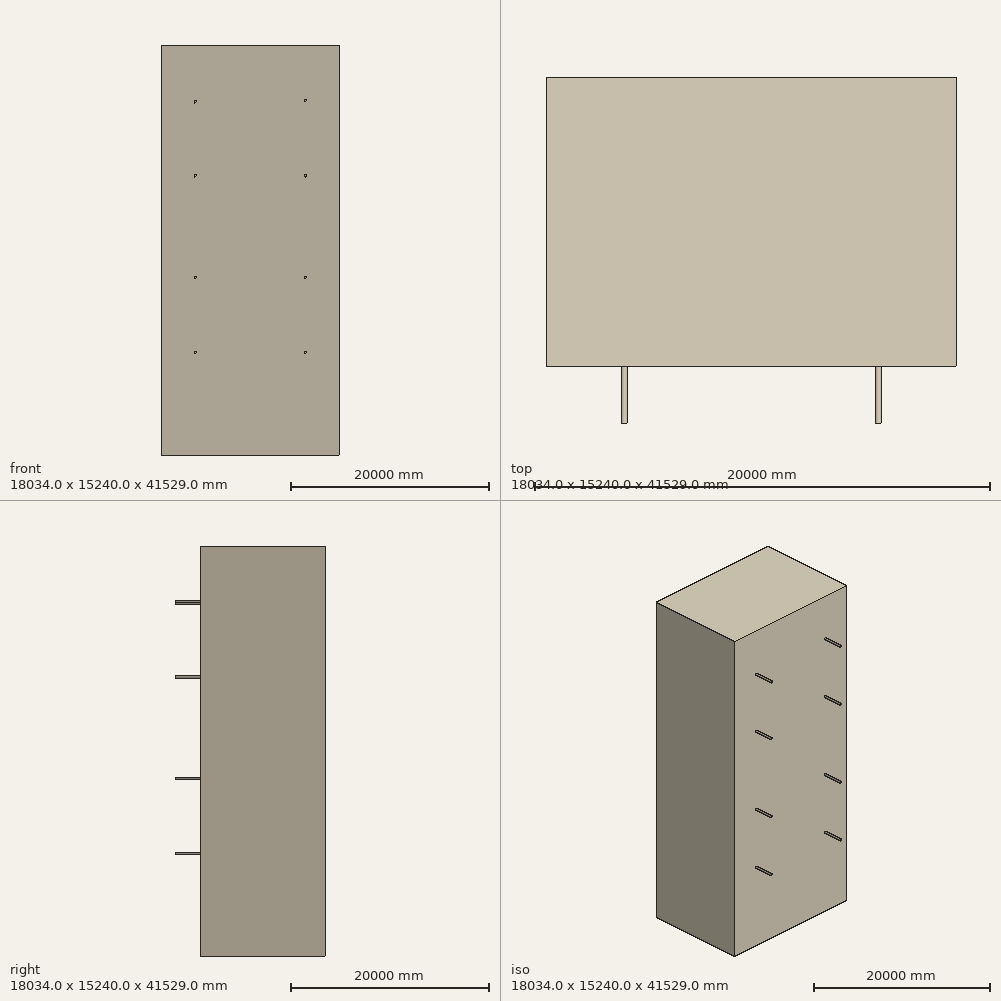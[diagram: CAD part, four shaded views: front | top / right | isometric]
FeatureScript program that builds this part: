
annotation { "Feature Type Name" : "Feature", "Feature Type Description" : "" }
export const myFeature = defineFeature(function(context is Context, id is Id, definition is map)
    precondition{}
    {
        {
            var Q0;
            Q0=qCreatedBy(makeId("Front.planeOp"),FACE);
            var sketch = newSketch(context, id + "F0", { "sketchPlane" : qUnion([Q0])});
            skLineSegment(sketch, "E0", {"start": v(0, 0) * mm, "end": v(18034, 0) * mm});
            skLineSegment(sketch, "E1", {"start": v(0, 0) * mm, "end": v(0, 41529) * mm});
            skLineSegment(sketch, "E2", {"start": v(0, 41529) * mm, "end": v(18034, 41529) * mm});
            skLineSegment(sketch, "E3", {"start": v(18034, 41529) * mm, "end": v(18034, 0) * mm});
            skSolve(sketch);
        }
        {
            var Q0;
            Q0=makeQuery(id+"F0.imprint","IMPRINT",FACE,{"disambiguationData":[TD([[makeQuery(id+"F0.imprint","IMPRINT",EDGE,{"derivedFrom":sQuery(id+"F0.wireOp",EDGE,"E0")}),1.0]])]});
            extrude(context, id + "F1", {"entities" : qUnion([Q0]), "depth" : 12700 * mm, "offsetDistance" : 25.4 * mm});
        }
        {
            var Q0;
            Q0=makeQuery(id+"F1.opExtrude","CAP_FACE",FACE,{"disambiguationData":[OSD([sQuery(id+"F0.wireOp",EDGE,"E0"),sQuery(id+"F0.wireOp",EDGE,"E1"),sQuery(id+"F0.wireOp",EDGE,"E2"),sQuery(id+"F0.wireOp",EDGE,"E3")])],"isStart":false});
            var sketch = newSketch(context, id + "F2", { "sketchPlane" : qUnion([Q0])});
            skCircle(sketch, "E4", {"center": v(3429, 35814) * mm, "radius": 127 * mm});
            skCircle(sketch, "E5", {"center": v(14605, 35941) * mm, "radius": 127 * mm});
            skCircle(sketch, "E6", {"center": v(3429, 28321) * mm, "radius": 127 * mm});
            skCircle(sketch, "E7", {"center": v(14605, 28321) * mm, "radius": 127 * mm});
            skCircle(sketch, "E8", {"center": v(3429, 18034) * mm, "radius": 127 * mm});
            skCircle(sketch, "E9", {"center": v(14605, 18034) * mm, "radius": 127 * mm});
            skCircle(sketch, "E10", {"center": v(3429, 10414) * mm, "radius": 127 * mm});
            skCircle(sketch, "E11", {"center": v(14605, 10414) * mm, "radius": 127 * mm});
            skSolve(sketch);
        }
        {
            var Q0;
            Q0 = qSketchRegion(id + "F2", true);
            extrude(context, id + "F3", {"entities" : qUnion([Q0]), "operationType" : NewBodyOperationType.ADD, "depth" : 2540 * mm, "offsetDistance" : 25.4 * mm});
        }
        {
            var Q0;
            Q0=makeQuery(id+"F1.opExtrude","CAP_FACE",FACE,{"disambiguationData":[OSD([sQuery(id+"F0.wireOp",EDGE,"E0"),sQuery(id+"F0.wireOp",EDGE,"E1"),sQuery(id+"F0.wireOp",EDGE,"E2"),sQuery(id+"F0.wireOp",EDGE,"E3")])],"isStart":true});
            var sketch = newSketch(context, id + "F4", { "sketchPlane" : qUnion([Q0])});
            skLineSegment(sketch, "E12.bottom", {"start": v(-16764, 17272) * mm, "end": v(-1270, 17272) * mm});
            skLineSegment(sketch, "E12.top", {"start": v(-16764, 2032) * mm, "end": v(-1270, 2032) * mm});
            skLineSegment(sketch, "E12.left", {"start": v(-16764, 17272) * mm, "end": v(-16764, 2032) * mm});
            skLineSegment(sketch, "E12.right", {"start": v(-1270, 17272) * mm, "end": v(-1270, 2032) * mm});
            skSolve(sketch);
        }
        {
            var Q0;
            Q0 = qSketchRegion(id + "F4", true);
            extrude(context, id + "F5", {"entities" : qUnion([Q0]), "operationType" : NewBodyOperationType.REMOVE, "oppositeDirection" : true, "depth" : 10160 * mm, "offsetDistance" : 25.4 * mm});
        }
    });
